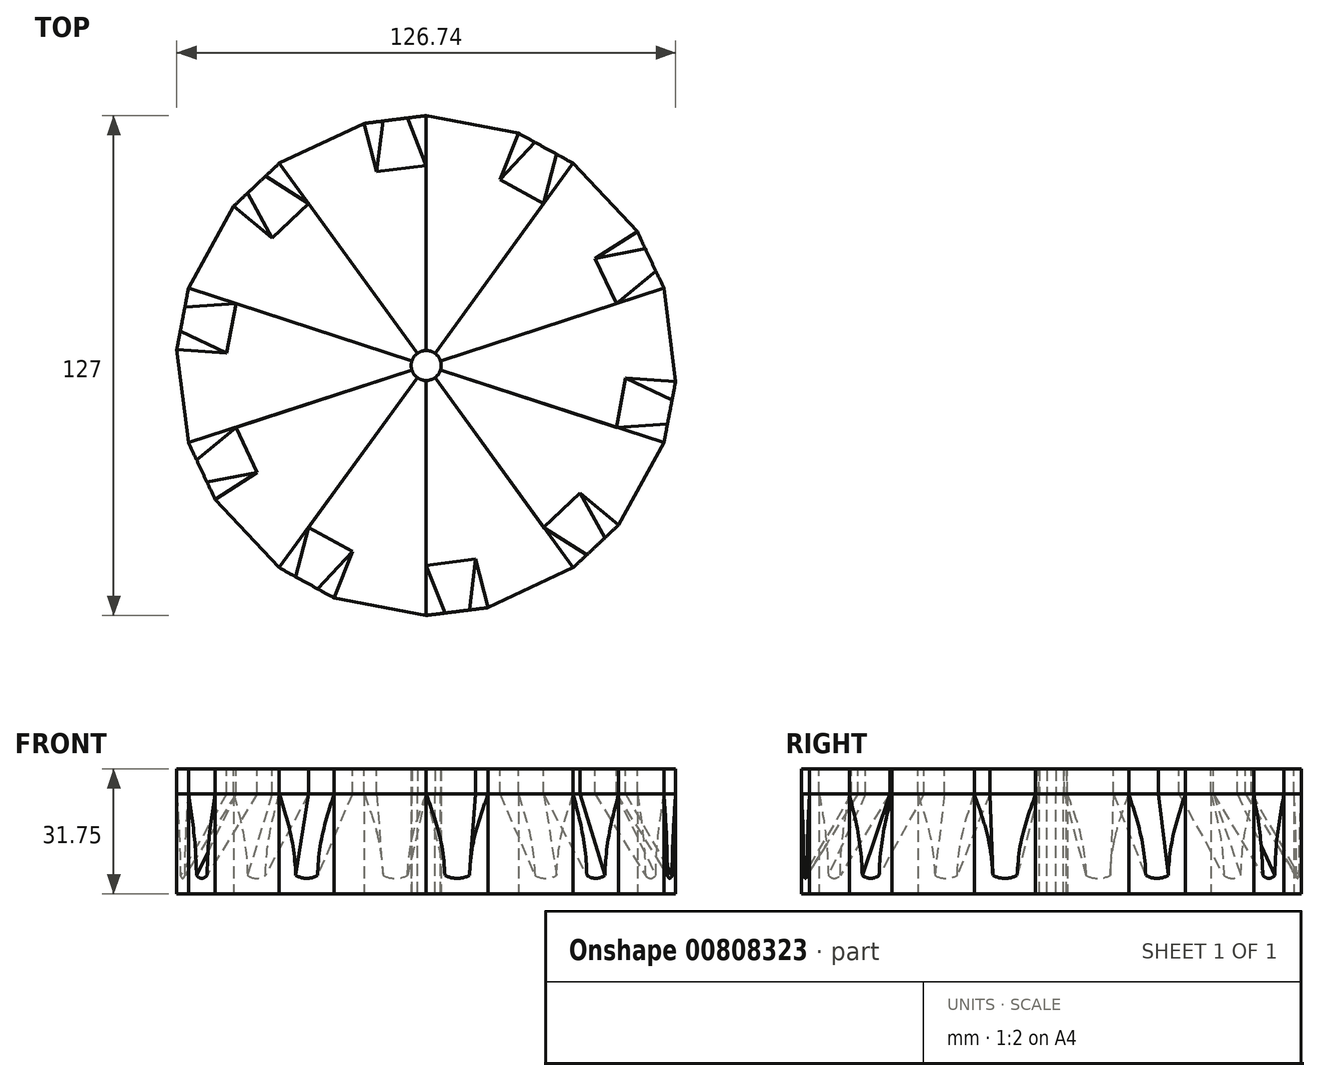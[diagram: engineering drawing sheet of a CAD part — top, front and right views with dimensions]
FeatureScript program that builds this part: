
annotation { "Feature Type Name" : "Feature", "Feature Type Description" : "" }
export const myFeature = defineFeature(function(context is Context, id is Id, definition is map)
    precondition{}
    {
        {
            var Q0;
            Q0=qCreatedBy(makeId("Top.planeOp"),FACE);
            var sketch = newSketch(context, id + "F0", { "sketchPlane" : qUnion([Q0])});
            skCircle(sketch, "E0", {"center": v(0, 0) * mm, "radius": 3.81 * mm});
            skCircle(sketch, "E1", {"center": v(0, 0) * mm, "radius": 63.5 * mm});
            skLineSegment(sketch, "E2", {"start": v(0, 0) * mm, "end": v(0, -3.81) * mm});
            skLineSegment(sketch, "E3", {"start": v(0, -50.8) * mm, "end": v(12.6, -49.21) * mm});
            skLineSegment(sketch, "E4", {"start": v(0, 0) * mm, "end": v(0.95, -3.7) * mm});
            skLineSegment(sketch, "E5", {"start": v(0, -63.5) * mm, "end": v(15.75, -61.52) * mm});
            skLineSegment(sketch, "E6.trimOffspring", {"start": v(0, -50.8) * mm, "end": v(0, -63.5) * mm});
            skLineSegment(sketch, "E7.trimOffspring", {"start": v(12.6, -49.21) * mm, "end": v(15.75, -61.52) * mm});
            skLineSegment(sketch, "E8.1.0", {"start": v(39.12, -32.4) * mm, "end": v(48.9, -40.5) * mm});
            skLineSegment(sketch, "E8.1.1", {"start": v(29.86, -41.1) * mm, "end": v(37.32, -51.37) * mm});
            skLineSegment(sketch, "E8.1.2", {"start": v(29.86, -41.1) * mm, "end": v(39.12, -32.4) * mm});
            skLineSegment(sketch, "E8.1.3", {"start": v(37.32, -51.37) * mm, "end": v(48.9, -40.5) * mm});
            skLineSegment(sketch, "E8.2.0", {"start": v(50.7, -3.22) * mm, "end": v(63.37, -4.03) * mm});
            skLineSegment(sketch, "E8.2.1", {"start": v(48.31, -15.7) * mm, "end": v(60.4, -19.62) * mm});
            skLineSegment(sketch, "E8.2.2", {"start": v(48.31, -15.7) * mm, "end": v(50.7, -3.22) * mm});
            skLineSegment(sketch, "E8.2.3", {"start": v(60.4, -19.62) * mm, "end": v(63.37, -4.03) * mm});
            skLineSegment(sketch, "E8.3.0", {"start": v(42.91, 27.2) * mm, "end": v(53.64, 33.99) * mm});
            skLineSegment(sketch, "E8.3.1", {"start": v(48.31, 15.7) * mm, "end": v(60.4, 19.62) * mm});
            skLineSegment(sketch, "E8.3.2", {"start": v(48.31, 15.7) * mm, "end": v(42.91, 27.2) * mm});
            skLineSegment(sketch, "E8.3.3", {"start": v(60.4, 19.62) * mm, "end": v(53.64, 33.99) * mm});
            skLineSegment(sketch, "E8.4.0", {"start": v(18.73, 47.22) * mm, "end": v(23.42, 59.03) * mm});
            skLineSegment(sketch, "E8.4.1", {"start": v(29.86, 41.1) * mm, "end": v(37.32, 51.37) * mm});
            skLineSegment(sketch, "E8.4.2", {"start": v(29.86, 41.1) * mm, "end": v(18.73, 47.22) * mm});
            skLineSegment(sketch, "E8.4.3", {"start": v(37.32, 51.37) * mm, "end": v(23.42, 59.03) * mm});
            skLineSegment(sketch, "E8.5.0", {"start": v(-12.6, 49.21) * mm, "end": v(-15.75, 61.52) * mm});
            skLineSegment(sketch, "E8.5.1", {"start": v(0, 50.8) * mm, "end": v(0, 63.5) * mm});
            skLineSegment(sketch, "E8.5.2", {"start": v(0, 50.8) * mm, "end": v(-12.6, 49.21) * mm});
            skLineSegment(sketch, "E8.5.3", {"start": v(0, 63.5) * mm, "end": v(-15.75, 61.52) * mm});
            skLineSegment(sketch, "E8.6.0", {"start": v(-39.12, 32.4) * mm, "end": v(-48.9, 40.5) * mm});
            skLineSegment(sketch, "E8.6.1", {"start": v(-29.86, 41.1) * mm, "end": v(-37.32, 51.37) * mm});
            skLineSegment(sketch, "E8.6.2", {"start": v(-29.86, 41.1) * mm, "end": v(-39.12, 32.4) * mm});
            skLineSegment(sketch, "E8.6.3", {"start": v(-37.32, 51.37) * mm, "end": v(-48.9, 40.5) * mm});
            skLineSegment(sketch, "E8.7.0", {"start": v(-50.7, 3.22) * mm, "end": v(-63.37, 4.03) * mm});
            skLineSegment(sketch, "E8.7.1", {"start": v(-48.31, 15.7) * mm, "end": v(-60.4, 19.62) * mm});
            skLineSegment(sketch, "E8.7.2", {"start": v(-48.31, 15.7) * mm, "end": v(-50.7, 3.22) * mm});
            skLineSegment(sketch, "E8.7.3", {"start": v(-60.4, 19.62) * mm, "end": v(-63.37, 4.03) * mm});
            skLineSegment(sketch, "E8.8.0", {"start": v(-42.91, -27.2) * mm, "end": v(-53.64, -33.99) * mm});
            skLineSegment(sketch, "E8.8.1", {"start": v(-48.31, -15.7) * mm, "end": v(-60.4, -19.62) * mm});
            skLineSegment(sketch, "E8.8.2", {"start": v(-48.31, -15.7) * mm, "end": v(-42.91, -27.2) * mm});
            skLineSegment(sketch, "E8.8.3", {"start": v(-60.4, -19.62) * mm, "end": v(-53.64, -33.99) * mm});
            skLineSegment(sketch, "E8.9.0", {"start": v(-18.73, -47.22) * mm, "end": v(-23.42, -59.03) * mm});
            skLineSegment(sketch, "E8.9.1", {"start": v(-29.86, -41.1) * mm, "end": v(-37.32, -51.37) * mm});
            skLineSegment(sketch, "E8.9.2", {"start": v(-29.86, -41.1) * mm, "end": v(-18.73, -47.22) * mm});
            skLineSegment(sketch, "E8.9.3", {"start": v(-37.32, -51.37) * mm, "end": v(-23.42, -59.03) * mm});
            skLineSegment(sketch, "E9", {"start": v(12.6, -49.21) * mm, "end": v(29.86, -41.1) * mm});
            skLineSegment(sketch, "E10", {"start": v(15.75, -61.52) * mm, "end": v(37.32, -51.37) * mm});
            skLineSegment(sketch, "E11.1.0", {"start": v(39.12, -32.4) * mm, "end": v(48.31, -15.7) * mm});
            skLineSegment(sketch, "E11.1.1", {"start": v(48.9, -40.5) * mm, "end": v(60.4, -19.62) * mm});
            skLineSegment(sketch, "E11.2.0", {"start": v(50.7, -3.22) * mm, "end": v(48.31, 15.7) * mm});
            skLineSegment(sketch, "E11.2.1", {"start": v(63.37, -4.03) * mm, "end": v(60.4, 19.62) * mm});
            skLineSegment(sketch, "E11.3.0", {"start": v(42.91, 27.2) * mm, "end": v(29.86, 41.1) * mm});
            skLineSegment(sketch, "E11.3.1", {"start": v(53.64, 33.99) * mm, "end": v(37.32, 51.37) * mm});
            skLineSegment(sketch, "E11.4.0", {"start": v(18.73, 47.22) * mm, "end": v(0, 50.8) * mm});
            skLineSegment(sketch, "E11.4.1", {"start": v(23.42, 59.03) * mm, "end": v(0, 63.5) * mm});
            skLineSegment(sketch, "E11.5.0", {"start": v(-12.6, 49.21) * mm, "end": v(-29.86, 41.1) * mm});
            skLineSegment(sketch, "E11.5.1", {"start": v(-15.75, 61.52) * mm, "end": v(-37.32, 51.37) * mm});
            skLineSegment(sketch, "E11.6.0", {"start": v(-39.12, 32.4) * mm, "end": v(-48.31, 15.7) * mm});
            skLineSegment(sketch, "E11.6.1", {"start": v(-48.9, 40.5) * mm, "end": v(-60.4, 19.62) * mm});
            skLineSegment(sketch, "E11.7.0", {"start": v(-50.7, 3.22) * mm, "end": v(-48.31, -15.7) * mm});
            skLineSegment(sketch, "E11.7.1", {"start": v(-63.37, 4.03) * mm, "end": v(-60.4, -19.62) * mm});
            skLineSegment(sketch, "E11.8.0", {"start": v(-42.91, -27.2) * mm, "end": v(-29.86, -41.1) * mm});
            skLineSegment(sketch, "E11.8.1", {"start": v(-53.64, -33.99) * mm, "end": v(-37.32, -51.37) * mm});
            skLineSegment(sketch, "E11.9.0", {"start": v(-18.73, -47.22) * mm, "end": v(0, -50.8) * mm});
            skLineSegment(sketch, "E11.9.1", {"start": v(-23.42, -59.03) * mm, "end": v(0, -63.5) * mm});
            skSolve(sketch);
        }
        {
            var Q0;
            Q0=makeQuery(id+"F0.imprint","IMPRINT",FACE,{"disambiguationData":[TD([[makeQuery(id+"F0.imprint","IMPRINT",EDGE,{"derivedFrom":sQuery(id+"F0.wireOp",EDGE,"E8.8.0")}),1.0]])]});
            var Q1;
            Q1=makeQuery(id+"F0.imprint","IMPRINT",FACE,{"disambiguationData":[TD([[makeQuery(id+"F0.imprint","IMPRINT",EDGE,{"derivedFrom":sQuery(id+"F0.wireOp",EDGE,"E8.7.0")}),1.0]])]});
            var Q2;
            Q2=makeQuery(id+"F0.imprint","IMPRINT",FACE,{"disambiguationData":[TD([[makeQuery(id+"F0.imprint","IMPRINT",EDGE,{"derivedFrom":sQuery(id+"F0.wireOp",EDGE,"E6.trimOffspring")}),-1.0]])]});
            var Q3;
            Q3=makeQuery(id+"F0.imprint","IMPRINT",FACE,{"disambiguationData":[TD([[makeQuery(id+"F0.imprint","IMPRINT",EDGE,{"derivedFrom":sQuery(id+"F0.wireOp",EDGE,"E7.trimOffspring")}),1.0]])]});
            var Q4;
            Q4=makeQuery(id+"F0.imprint","IMPRINT",FACE,{"disambiguationData":[TD([[makeQuery(id+"F0.imprint","IMPRINT",EDGE,{"derivedFrom":sQuery(id+"F0.wireOp",EDGE,"E8.1.0")}),1.0]])]});
            var Q5;
            Q5=makeQuery(id+"F0.imprint","IMPRINT",FACE,{"disambiguationData":[TD([[makeQuery(id+"F0.imprint","IMPRINT",EDGE,{"derivedFrom":sQuery(id+"F0.wireOp",EDGE,"E8.2.0")}),1.0]])]});
            var Q6;
            Q6=makeQuery(id+"F0.imprint","IMPRINT",FACE,{"disambiguationData":[TD([[makeQuery(id+"F0.imprint","IMPRINT",EDGE,{"derivedFrom":sQuery(id+"F0.wireOp",EDGE,"E8.3.0")}),1.0]])]});
            var Q7;
            Q7=makeQuery(id+"F0.imprint","IMPRINT",FACE,{"disambiguationData":[TD([[makeQuery(id+"F0.imprint","IMPRINT",EDGE,{"derivedFrom":sQuery(id+"F0.wireOp",EDGE,"E8.4.0")}),1.0]])]});
            var Q8;
            Q8=makeQuery(id+"F0.imprint","IMPRINT",FACE,{"disambiguationData":[TD([[makeQuery(id+"F0.imprint","IMPRINT",EDGE,{"derivedFrom":sQuery(id+"F0.wireOp",EDGE,"E8.5.0")}),1.0]])]});
            var Q9;
            Q9=makeQuery(id+"F0.imprint","IMPRINT",FACE,{"disambiguationData":[TD([[makeQuery(id+"F0.imprint","IMPRINT",EDGE,{"derivedFrom":sQuery(id+"F0.wireOp",EDGE,"E8.6.0")}),1.0]])]});
            var Q10;
            Q10=makeQuery(id+"F0.imprint","IMPRINT",FACE,{"disambiguationData":[TD([[makeQuery(id+"F0.imprint","IMPRINT",EDGE,{"derivedFrom":sQuery(id+"F0.wireOp",EDGE,"E3")}),1.0]])]});
            var Q11;
            Q11=makeQuery(id+"F0.imprint","IMPRINT",FACE,{"disambiguationData":[TD([[makeQuery(id+"F0.imprint","IMPRINT",EDGE,{"derivedFrom":sQuery(id+"F0.wireOp",EDGE,"E3")}),-1.0]])]});
            var Q12;
            Q12=makeQuery(id+"F0.imprint","IMPRINT",FACE,{"disambiguationData":[TD([[makeQuery(id+"F0.imprint","IMPRINT",EDGE,{"derivedFrom":sQuery(id+"F0.wireOp",EDGE,"E8.9.0")}),-1.0]])]});
            var Q13;
            Q13=makeQuery(id+"F0.imprint","IMPRINT",FACE,{"disambiguationData":[TD([[makeQuery(id+"F0.imprint","IMPRINT",EDGE,{"derivedFrom":sQuery(id+"F0.wireOp",EDGE,"E8.1.0")}),-1.0]])]});
            var Q14;
            Q14=makeQuery(id+"F0.imprint","IMPRINT",FACE,{"disambiguationData":[TD([[makeQuery(id+"F0.imprint","IMPRINT",EDGE,{"derivedFrom":sQuery(id+"F0.wireOp",EDGE,"E8.2.0")}),-1.0]])]});
            var Q15;
            Q15=makeQuery(id+"F0.imprint","IMPRINT",FACE,{"disambiguationData":[TD([[makeQuery(id+"F0.imprint","IMPRINT",EDGE,{"derivedFrom":sQuery(id+"F0.wireOp",EDGE,"E8.3.0")}),-1.0]])]});
            var Q16;
            Q16=makeQuery(id+"F0.imprint","IMPRINT",FACE,{"disambiguationData":[TD([[makeQuery(id+"F0.imprint","IMPRINT",EDGE,{"derivedFrom":sQuery(id+"F0.wireOp",EDGE,"E8.8.0")}),-1.0]])]});
            var Q17;
            Q17=makeQuery(id+"F0.imprint","IMPRINT",FACE,{"disambiguationData":[TD([[makeQuery(id+"F0.imprint","IMPRINT",EDGE,{"derivedFrom":sQuery(id+"F0.wireOp",EDGE,"E8.7.0")}),-1.0]])]});
            var Q18;
            Q18=makeQuery(id+"F0.imprint","IMPRINT",FACE,{"disambiguationData":[TD([[makeQuery(id+"F0.imprint","IMPRINT",EDGE,{"derivedFrom":sQuery(id+"F0.wireOp",EDGE,"E8.6.0")}),-1.0]])]});
            var Q19;
            Q19=makeQuery(id+"F0.imprint","IMPRINT",FACE,{"disambiguationData":[TD([[makeQuery(id+"F0.imprint","IMPRINT",EDGE,{"derivedFrom":sQuery(id+"F0.wireOp",EDGE,"E8.5.0")}),-1.0]])]});
            var Q20;
            Q20=makeQuery(id+"F0.imprint","IMPRINT",FACE,{"disambiguationData":[TD([[makeQuery(id+"F0.imprint","IMPRINT",EDGE,{"derivedFrom":sQuery(id+"F0.wireOp",EDGE,"E8.4.0")}),-1.0]])]});
            extrude(context, id + "F1", {"entities" : qUnion([Q0, Q1, Q2, Q3, Q4, Q5, Q6, Q7, Q8, Q9, Q10, Q11, Q12, Q13, Q14, Q15, Q16, Q17, Q18, Q19, Q20]), "depth" : 25.4 * mm, "offsetDistance" : 25.4 * mm});
        }
        {
            var Q0;
            Q0=makeQuery(id+"F1.opExtrude","CAP_EDGE",EDGE,{"disambiguationData":[OSD([sQuery(id+"F0.wireOp",EDGE,"E5")])],"isStart":false});
            cPoint(context, id + "F2", {"entities" : qUnion([Q0]), "parameter" : 0.5});
        }
        {
            var Q0;
            Q0=makeQuery(id+"F1.opExtrude","CAP_VERTEX",VERTEX,{"disambiguationData":[OSD([sQuery(id+"F0.wireOp",EDGE,"E1"),sQuery(id+"F0.wireOp",EDGE,"E5"),sQuery(id+"F0.wireOp",EDGE,"E7.trimOffspring"),sQuery(id+"F0.wireOp",EDGE,"E10")])],"isStart":true});
            var Q1;
            Q1=makeQuery(id+"F1.opExtrude","CAP_VERTEX",VERTEX,{"disambiguationData":[OSD([sQuery(id+"F0.wireOp",EDGE,"E1"),sQuery(id+"F0.wireOp",EDGE,"E5"),sQuery(id+"F0.wireOp",EDGE,"E6.trimOffspring"),sQuery(id+"F0.wireOp",EDGE,"E11.9.1")])],"isStart":true});
            var Q2;
            Q2 = qCreatedBy(id + "F2" ,VERTEX);
            cPlane(context, id + "F3", {"entities" : qUnion([Q0, Q1, Q2]), "cplaneType" : CPlaneType.THREE_POINT, "offset" : 25.4 * mm, "width" : 152.4 * mm, "height" : 152.4 * mm});
        }
        {
            var Q0;
            Q0=qCreatedBy(id+"F3.planeOp",FACE);
            cPlane(context, id + "F4", {"entities" : qUnion([Q0]), "cplaneType" : CPlaneType.OFFSET, "offset" : 1.59 * mm, "width" : 152.4 * mm, "height" : 152.4 * mm});
        }
        {
            var Q0;
            Q0=qCreatedBy(id+"F4.planeOp",FACE);
            var sketch = newSketch(context, id + "F5", { "sketchPlane" : qUnion([Q0])});
            skPoint(sketch, "E12.0", {"position": v(7.94, 12.7) * mm});
            skPoint(sketch, "E13.0", {"position": v(-7.94, 12.7) * mm});
            skPoint(sketch, "E14.0", {"position": v(0, 0) * mm});
            skLineSegment(sketch, "E15", {"start": v(0, 0) * mm, "end": v(0, 6.35) * mm});
            skLineSegment(sketch, "E16.bottom", {"start": v(2.74, 10.62) * mm, "end": v(-2.74, 10.62) * mm});
            skLineSegment(sketch, "E16.left", {"start": v(2.74, 10.62) * mm, "end": v(2.74, 2.08) * mm});
            skLineSegment(sketch, "E16.right", {"start": v(-2.74, 10.62) * mm, "end": v(-2.74, 2.08) * mm});
            skPoint(sketch, "E16.middle", {"position": v(0, 6.35) * mm});
            skArc(sketch, "E17.trimOffspring", {"start": v(-2.74, 2.08) * mm, "mid": v(0, 1.27) * mm, "end": v(2.74, 2.08) * mm});
            skSolve(sketch);
        }
        {
            var Q0;
            Q0=makeQuery(id+"F1.opExtrude","CAP_FACE",FACE,{"disambiguationData":[OSD([sQuery(id+"F0.wireOp",EDGE,"E0"),sQuery(id+"F0.wireOp",EDGE,"E5"),sQuery(id+"F0.wireOp",EDGE,"E8.1.3"),sQuery(id+"F0.wireOp",EDGE,"E8.2.3"),sQuery(id+"F0.wireOp",EDGE,"E8.3.3"),sQuery(id+"F0.wireOp",EDGE,"E8.4.3"),sQuery(id+"F0.wireOp",EDGE,"E8.5.3"),sQuery(id+"F0.wireOp",EDGE,"E8.6.3"),sQuery(id+"F0.wireOp",EDGE,"E8.7.3"),sQuery(id+"F0.wireOp",EDGE,"E8.8.3"),sQuery(id+"F0.wireOp",EDGE,"E8.9.3"),sQuery(id+"F0.wireOp",EDGE,"E10"),sQuery(id+"F0.wireOp",EDGE,"E11.1.1"),sQuery(id+"F0.wireOp",EDGE,"E11.2.1"),sQuery(id+"F0.wireOp",EDGE,"E11.3.1"),sQuery(id+"F0.wireOp",EDGE,"E11.4.1"),sQuery(id+"F0.wireOp",EDGE,"E11.5.1"),sQuery(id+"F0.wireOp",EDGE,"E11.6.1"),sQuery(id+"F0.wireOp",EDGE,"E11.7.1"),sQuery(id+"F0.wireOp",EDGE,"E11.8.1"),sQuery(id+"F0.wireOp",EDGE,"E11.9.1")])],"isStart":false});
            var sketch = newSketch(context, id + "F6", { "sketchPlane" : qUnion([Q0])});
            skLineSegment(sketch, "E18.0", {"start": v(37.32, -51.37) * mm, "end": v(48.9, -40.5) * mm});
            skLineSegment(sketch, "E18.1", {"start": v(29.86, -41.1) * mm, "end": v(39.12, -32.4) * mm});
            skLineSegment(sketch, "E18.2", {"start": v(-18.73, -47.22) * mm, "end": v(0, -50.8) * mm});
            skLineSegment(sketch, "E18.3", {"start": v(-48.31, 15.7) * mm, "end": v(-60.4, 19.62) * mm});
            skLineSegment(sketch, "E18.4", {"start": v(60.4, -19.62) * mm, "end": v(63.37, -4.03) * mm});
            skLineSegment(sketch, "E18.5", {"start": v(63.37, -4.03) * mm, "end": v(60.4, 19.62) * mm});
            skLineSegment(sketch, "E18.6", {"start": v(12.6, -49.21) * mm, "end": v(15.75, -61.52) * mm});
            skLineSegment(sketch, "E18.7", {"start": v(-50.7, 3.22) * mm, "end": v(-48.31, -15.7) * mm});
            skLineSegment(sketch, "E18.8", {"start": v(0, -50.8) * mm, "end": v(0, -63.5) * mm});
            skLineSegment(sketch, "E18.9", {"start": v(0, -63.5) * mm, "end": v(15.75, -61.52) * mm});
            skLineSegment(sketch, "E18.10", {"start": v(0, -50.8) * mm, "end": v(12.6, -49.21) * mm});
            skCircle(sketch, "E18.11", {"center": v(0, 0) * mm, "radius": 63.5 * mm});
            skLineSegment(sketch, "E18.12", {"start": v(50.7, -3.22) * mm, "end": v(63.37, -4.03) * mm});
            skLineSegment(sketch, "E18.13", {"start": v(42.91, 27.2) * mm, "end": v(53.64, 33.99) * mm});
            skLineSegment(sketch, "E18.14", {"start": v(48.31, -15.7) * mm, "end": v(50.7, -3.22) * mm});
            skLineSegment(sketch, "E18.15", {"start": v(-48.31, -15.7) * mm, "end": v(-42.91, -27.2) * mm});
            skLineSegment(sketch, "E18.16", {"start": v(0, 50.8) * mm, "end": v(-12.6, 49.21) * mm});
            skLineSegment(sketch, "E18.17", {"start": v(48.31, -15.7) * mm, "end": v(60.4, -19.62) * mm});
            skLineSegment(sketch, "E18.18", {"start": v(-37.32, 51.37) * mm, "end": v(-48.9, 40.5) * mm});
            skLineSegment(sketch, "E18.19", {"start": v(48.31, 15.7) * mm, "end": v(60.4, 19.62) * mm});
            skLineSegment(sketch, "E18.20", {"start": v(29.86, 41.1) * mm, "end": v(37.32, 51.37) * mm});
            skLineSegment(sketch, "E18.21", {"start": v(-12.6, 49.21) * mm, "end": v(-15.75, 61.52) * mm});
            skLineSegment(sketch, "E18.22", {"start": v(-18.73, -47.22) * mm, "end": v(-23.42, -59.03) * mm});
            skLineSegment(sketch, "E18.23", {"start": v(60.4, 19.62) * mm, "end": v(53.64, 33.99) * mm});
            skLineSegment(sketch, "E18.24", {"start": v(-39.12, 32.4) * mm, "end": v(-48.31, 15.7) * mm});
            skLineSegment(sketch, "E18.25", {"start": v(-23.42, -59.03) * mm, "end": v(0, -63.5) * mm});
            skLineSegment(sketch, "E18.26", {"start": v(-12.6, 49.21) * mm, "end": v(-29.86, 41.1) * mm});
            skLineSegment(sketch, "E18.27", {"start": v(-15.75, 61.52) * mm, "end": v(-37.32, 51.37) * mm});
            skLineSegment(sketch, "E18.28", {"start": v(-50.7, 3.22) * mm, "end": v(-63.37, 4.03) * mm});
            skLineSegment(sketch, "E18.29", {"start": v(50.7, -3.22) * mm, "end": v(48.31, 15.7) * mm});
            skLineSegment(sketch, "E18.30", {"start": v(12.6, -49.21) * mm, "end": v(29.86, -41.1) * mm});
            skLineSegment(sketch, "E18.31", {"start": v(48.9, -40.5) * mm, "end": v(60.4, -19.62) * mm});
            skLineSegment(sketch, "E18.32", {"start": v(-29.86, -41.1) * mm, "end": v(-18.73, -47.22) * mm});
            skLineSegment(sketch, "E18.33", {"start": v(-48.31, 15.7) * mm, "end": v(-50.7, 3.22) * mm});
            skLineSegment(sketch, "E18.34", {"start": v(-39.12, 32.4) * mm, "end": v(-48.9, 40.5) * mm});
            skLineSegment(sketch, "E18.35", {"start": v(42.91, 27.2) * mm, "end": v(29.86, 41.1) * mm});
            skLineSegment(sketch, "E18.36", {"start": v(-48.31, -15.7) * mm, "end": v(-60.4, -19.62) * mm});
            skLineSegment(sketch, "E18.37", {"start": v(29.86, 41.1) * mm, "end": v(18.73, 47.22) * mm});
            skLineSegment(sketch, "E18.38", {"start": v(37.32, 51.37) * mm, "end": v(23.42, 59.03) * mm});
            skLineSegment(sketch, "E18.39", {"start": v(-60.4, -19.62) * mm, "end": v(-53.64, -33.99) * mm});
            skLineSegment(sketch, "E18.40", {"start": v(-29.86, 41.1) * mm, "end": v(-39.12, 32.4) * mm});
            skLineSegment(sketch, "E18.41", {"start": v(23.42, 59.03) * mm, "end": v(0, 63.5) * mm});
            skLineSegment(sketch, "E18.42", {"start": v(39.12, -32.4) * mm, "end": v(48.31, -15.7) * mm});
            skLineSegment(sketch, "E18.43", {"start": v(39.12, -32.4) * mm, "end": v(48.9, -40.5) * mm});
            skLineSegment(sketch, "E18.44", {"start": v(-42.91, -27.2) * mm, "end": v(-29.86, -41.1) * mm});
            skLineSegment(sketch, "E18.45", {"start": v(29.86, -41.1) * mm, "end": v(37.32, -51.37) * mm});
            skLineSegment(sketch, "E18.46", {"start": v(53.64, 33.99) * mm, "end": v(37.32, 51.37) * mm});
            skCircle(sketch, "E18.47", {"center": v(0, 0) * mm, "radius": 3.81 * mm});
            skLineSegment(sketch, "E18.48", {"start": v(-48.9, 40.5) * mm, "end": v(-60.4, 19.62) * mm});
            skLineSegment(sketch, "E18.49", {"start": v(48.31, 15.7) * mm, "end": v(42.91, 27.2) * mm});
            skLineSegment(sketch, "E18.50", {"start": v(0, 50.8) * mm, "end": v(0, 63.5) * mm});
            skLineSegment(sketch, "E18.51", {"start": v(-29.86, -41.1) * mm, "end": v(-37.32, -51.37) * mm});
            skLineSegment(sketch, "E18.52", {"start": v(-29.86, 41.1) * mm, "end": v(-37.32, 51.37) * mm});
            skLineSegment(sketch, "E18.53", {"start": v(-42.91, -27.2) * mm, "end": v(-53.64, -33.99) * mm});
            skLineSegment(sketch, "E18.54", {"start": v(15.75, -61.52) * mm, "end": v(37.32, -51.37) * mm});
            skLineSegment(sketch, "E18.55", {"start": v(18.73, 47.22) * mm, "end": v(0, 50.8) * mm});
            skLineSegment(sketch, "E18.56", {"start": v(-53.64, -33.99) * mm, "end": v(-37.32, -51.37) * mm});
            skLineSegment(sketch, "E18.57", {"start": v(18.73, 47.22) * mm, "end": v(23.42, 59.03) * mm});
            skLineSegment(sketch, "E18.58", {"start": v(0, 63.5) * mm, "end": v(-15.75, 61.52) * mm});
            skLineSegment(sketch, "E18.59", {"start": v(-37.32, -51.37) * mm, "end": v(-23.42, -59.03) * mm});
            skLineSegment(sketch, "E18.60", {"start": v(-63.37, 4.03) * mm, "end": v(-60.4, -19.62) * mm});
            skLineSegment(sketch, "E18.61", {"start": v(-60.4, 19.62) * mm, "end": v(-63.37, 4.03) * mm});
            skSolve(sketch);
        }
        {
            var Q1;
            Q1=makeQuery(id+"F6.imprint","IMPRINT",FACE,{"disambiguationData":[TD([[makeQuery(id+"F6.imprint","IMPRINT",EDGE,{"derivedFrom":sQuery(id+"F6.wireOp",EDGE,"E18.6")}),-1.0]])]});
            var Q2;
            Q2=makeQuery(id+"F5.imprint","IMPRINT",FACE,{"disambiguationData":[TD([[makeQuery(id+"F5.imprint","IMPRINT",EDGE,{"derivedFrom":sQuery(id+"F5.wireOp",EDGE,"E16.bottom")}),1.0]])]});
            loft(context, id + "F7", {"operationType" : NewBodyOperationType.REMOVE, "sheetProfilesArray" : [{ "sheetProfileEntities" : qUnion([Q1]) }, { "sheetProfileEntities" : qUnion([Q2]) }]});
        }
        {
            var Q0;
            Q0=makeQuery(id+"F1.opExtrude","CAP_FACE",FACE,{"disambiguationData":[OSD([sQuery(id+"F0.wireOp",EDGE,"E0"),sQuery(id+"F0.wireOp",EDGE,"E5"),sQuery(id+"F0.wireOp",EDGE,"E8.1.3"),sQuery(id+"F0.wireOp",EDGE,"E8.2.3"),sQuery(id+"F0.wireOp",EDGE,"E8.3.3"),sQuery(id+"F0.wireOp",EDGE,"E8.4.3"),sQuery(id+"F0.wireOp",EDGE,"E8.5.3"),sQuery(id+"F0.wireOp",EDGE,"E8.6.3"),sQuery(id+"F0.wireOp",EDGE,"E8.7.3"),sQuery(id+"F0.wireOp",EDGE,"E8.8.3"),sQuery(id+"F0.wireOp",EDGE,"E8.9.3"),sQuery(id+"F0.wireOp",EDGE,"E10"),sQuery(id+"F0.wireOp",EDGE,"E11.1.1"),sQuery(id+"F0.wireOp",EDGE,"E11.2.1"),sQuery(id+"F0.wireOp",EDGE,"E11.3.1"),sQuery(id+"F0.wireOp",EDGE,"E11.4.1"),sQuery(id+"F0.wireOp",EDGE,"E11.5.1"),sQuery(id+"F0.wireOp",EDGE,"E11.6.1"),sQuery(id+"F0.wireOp",EDGE,"E11.7.1"),sQuery(id+"F0.wireOp",EDGE,"E11.8.1"),sQuery(id+"F0.wireOp",EDGE,"E11.9.1")])],"isStart":false});
            var sketch = newSketch(context, id + "F8", { "sketchPlane" : qUnion([Q0])});
            skLineSegment(sketch, "E19", {"start": v(0, -63.5) * mm, "end": v(0, 0) * mm});
            skLineSegment(sketch, "E20", {"start": v(0, 0) * mm, "end": v(37.32, -51.37) * mm});
            skSolve(sketch);
        }
        {
            var Q0;
            Q0 = qSketchRegion(id + "F8", true);
            var Q1;
            {var subQ0=sQuery(id+"F8.wireOp",EDGE,"E20");var subQ1=sQuery(id+"F8.wireOp",EDGE,"E19");var subQ2=makeQuery(id+"F8.imprint","INTERSECT",VERTEX,{"derivedFrom":[subQ1,subQ0]});Q1=makeQuery(id+"F8.imprint","IMPRINT",FACE,{"disambiguationData":[TD([[makeQuery(id+"F8.imprint","IMPRINT",EDGE,{"disambiguationData":[TD([[subQ2,1.0]])],"derivedFrom":subQ1}),1.0]])]});}
            var Q2;
            {var subQ5=makeQuery(id+"F1.opExtrude","CAP_EDGE",EDGE,{"disambiguationData":[OSD([sQuery(id+"F0.wireOp",EDGE,"E8.1.3")])],"isStart":false});Q2=makeQuery(id+"F8.imprint","IMPRINT",FACE,{"disambiguationData":[TD([[makeQuery(id+"F8.imprint","IMPRINT",EDGE,{"derivedFrom":subQ5}),1.0]])]});}
            var Q3;
            {var subQ0=sQuery(id+"F8.wireOp",EDGE,"E20");var subQ1=sQuery(id+"F8.wireOp",EDGE,"E19");var subQ2=makeQuery(id+"F8.imprint","INTERSECT",VERTEX,{"derivedFrom":[subQ1,subQ0]});Q3=makeQuery(id+"F8.imprint","IMPRINT",FACE,{"disambiguationData":[TD([[makeQuery(id+"F8.imprint","IMPRINT",EDGE,{"disambiguationData":[TD([[subQ2,1.0]])],"derivedFrom":subQ1}),-1.0]])]});}
            extrude(context, id + "F9", {"entities" : qUnion([Q0, Q1, Q2, Q3]), "operationType" : NewBodyOperationType.REMOVE, "oppositeDirection" : true, "depth" : 25.4 * mm, "offsetDistance" : 25.4 * mm});
        }
        {
            var Q0;
            Q0=makeQuery(id+"F1.opExtrude","SWEPT_BODY",BODY,{"disambiguationData":[OSD([sQuery(id+"F0.wireOp",EDGE,"E0"),sQuery(id+"F0.wireOp",EDGE,"E5"),sQuery(id+"F0.wireOp",EDGE,"E8.1.3"),sQuery(id+"F0.wireOp",EDGE,"E8.2.3"),sQuery(id+"F0.wireOp",EDGE,"E8.3.3"),sQuery(id+"F0.wireOp",EDGE,"E8.4.3"),sQuery(id+"F0.wireOp",EDGE,"E8.5.3"),sQuery(id+"F0.wireOp",EDGE,"E8.6.3"),sQuery(id+"F0.wireOp",EDGE,"E8.7.3"),sQuery(id+"F0.wireOp",EDGE,"E8.8.3"),sQuery(id+"F0.wireOp",EDGE,"E8.9.3"),sQuery(id+"F0.wireOp",EDGE,"E10"),sQuery(id+"F0.wireOp",EDGE,"E11.1.1"),sQuery(id+"F0.wireOp",EDGE,"E11.2.1"),sQuery(id+"F0.wireOp",EDGE,"E11.3.1"),sQuery(id+"F0.wireOp",EDGE,"E11.4.1"),sQuery(id+"F0.wireOp",EDGE,"E11.5.1"),sQuery(id+"F0.wireOp",EDGE,"E11.6.1"),sQuery(id+"F0.wireOp",EDGE,"E11.7.1"),sQuery(id+"F0.wireOp",EDGE,"E11.8.1"),sQuery(id+"F0.wireOp",EDGE,"E11.9.1")])]});
            var Q1;
            Q1=makeQuery(id+"F1.opExtrude","SWEPT_FACE",FACE,{"disambiguationData":[OSD([sQuery(id+"F0.wireOp",EDGE,"E0")])]});
            circularPattern(context, id + "F10", {"entities" : qUnion([Q0]), "axis" : qUnion([Q1]), "angle" : 360 * degree, "instanceCount" : 10, "equalSpace" : true});
        }
        {
            var Q0;
            Q0=makeQuery(id+"F10.opPattern","COPY",FACE,{"derivedFrom":makeQuery(id+"F1.opExtrude","CAP_FACE",FACE,{"disambiguationData":[OSD([sQuery(id+"F0.wireOp",EDGE,"E0"),sQuery(id+"F0.wireOp",EDGE,"E5"),sQuery(id+"F0.wireOp",EDGE,"E8.1.3"),sQuery(id+"F0.wireOp",EDGE,"E8.2.3"),sQuery(id+"F0.wireOp",EDGE,"E8.3.3"),sQuery(id+"F0.wireOp",EDGE,"E8.4.3"),sQuery(id+"F0.wireOp",EDGE,"E8.5.3"),sQuery(id+"F0.wireOp",EDGE,"E8.6.3"),sQuery(id+"F0.wireOp",EDGE,"E8.7.3"),sQuery(id+"F0.wireOp",EDGE,"E8.8.3"),sQuery(id+"F0.wireOp",EDGE,"E8.9.3"),sQuery(id+"F0.wireOp",EDGE,"E10"),sQuery(id+"F0.wireOp",EDGE,"E11.1.1"),sQuery(id+"F0.wireOp",EDGE,"E11.2.1"),sQuery(id+"F0.wireOp",EDGE,"E11.3.1"),sQuery(id+"F0.wireOp",EDGE,"E11.4.1"),sQuery(id+"F0.wireOp",EDGE,"E11.5.1"),sQuery(id+"F0.wireOp",EDGE,"E11.6.1"),sQuery(id+"F0.wireOp",EDGE,"E11.7.1"),sQuery(id+"F0.wireOp",EDGE,"E11.8.1"),sQuery(id+"F0.wireOp",EDGE,"E11.9.1")])],"isStart":false}),"instanceName":"7"});
            var Q1;
            Q1=makeQuery(id+"F10.opPattern","COPY",FACE,{"derivedFrom":makeQuery(id+"F1.opExtrude","CAP_FACE",FACE,{"disambiguationData":[OSD([sQuery(id+"F0.wireOp",EDGE,"E0"),sQuery(id+"F0.wireOp",EDGE,"E5"),sQuery(id+"F0.wireOp",EDGE,"E8.1.3"),sQuery(id+"F0.wireOp",EDGE,"E8.2.3"),sQuery(id+"F0.wireOp",EDGE,"E8.3.3"),sQuery(id+"F0.wireOp",EDGE,"E8.4.3"),sQuery(id+"F0.wireOp",EDGE,"E8.5.3"),sQuery(id+"F0.wireOp",EDGE,"E8.6.3"),sQuery(id+"F0.wireOp",EDGE,"E8.7.3"),sQuery(id+"F0.wireOp",EDGE,"E8.8.3"),sQuery(id+"F0.wireOp",EDGE,"E8.9.3"),sQuery(id+"F0.wireOp",EDGE,"E10"),sQuery(id+"F0.wireOp",EDGE,"E11.1.1"),sQuery(id+"F0.wireOp",EDGE,"E11.2.1"),sQuery(id+"F0.wireOp",EDGE,"E11.3.1"),sQuery(id+"F0.wireOp",EDGE,"E11.4.1"),sQuery(id+"F0.wireOp",EDGE,"E11.5.1"),sQuery(id+"F0.wireOp",EDGE,"E11.6.1"),sQuery(id+"F0.wireOp",EDGE,"E11.7.1"),sQuery(id+"F0.wireOp",EDGE,"E11.8.1"),sQuery(id+"F0.wireOp",EDGE,"E11.9.1")])],"isStart":false}),"instanceName":"6"});
            var Q2;
            Q2=makeQuery(id+"F10.opPattern","COPY",FACE,{"derivedFrom":makeQuery(id+"F1.opExtrude","CAP_FACE",FACE,{"disambiguationData":[OSD([sQuery(id+"F0.wireOp",EDGE,"E0"),sQuery(id+"F0.wireOp",EDGE,"E5"),sQuery(id+"F0.wireOp",EDGE,"E8.1.3"),sQuery(id+"F0.wireOp",EDGE,"E8.2.3"),sQuery(id+"F0.wireOp",EDGE,"E8.3.3"),sQuery(id+"F0.wireOp",EDGE,"E8.4.3"),sQuery(id+"F0.wireOp",EDGE,"E8.5.3"),sQuery(id+"F0.wireOp",EDGE,"E8.6.3"),sQuery(id+"F0.wireOp",EDGE,"E8.7.3"),sQuery(id+"F0.wireOp",EDGE,"E8.8.3"),sQuery(id+"F0.wireOp",EDGE,"E8.9.3"),sQuery(id+"F0.wireOp",EDGE,"E10"),sQuery(id+"F0.wireOp",EDGE,"E11.1.1"),sQuery(id+"F0.wireOp",EDGE,"E11.2.1"),sQuery(id+"F0.wireOp",EDGE,"E11.3.1"),sQuery(id+"F0.wireOp",EDGE,"E11.4.1"),sQuery(id+"F0.wireOp",EDGE,"E11.5.1"),sQuery(id+"F0.wireOp",EDGE,"E11.6.1"),sQuery(id+"F0.wireOp",EDGE,"E11.7.1"),sQuery(id+"F0.wireOp",EDGE,"E11.8.1"),sQuery(id+"F0.wireOp",EDGE,"E11.9.1")])],"isStart":false}),"instanceName":"5"});
            var Q3;
            Q3=makeQuery(id+"F10.opPattern","COPY",FACE,{"derivedFrom":makeQuery(id+"F1.opExtrude","CAP_FACE",FACE,{"disambiguationData":[OSD([sQuery(id+"F0.wireOp",EDGE,"E0"),sQuery(id+"F0.wireOp",EDGE,"E5"),sQuery(id+"F0.wireOp",EDGE,"E8.1.3"),sQuery(id+"F0.wireOp",EDGE,"E8.2.3"),sQuery(id+"F0.wireOp",EDGE,"E8.3.3"),sQuery(id+"F0.wireOp",EDGE,"E8.4.3"),sQuery(id+"F0.wireOp",EDGE,"E8.5.3"),sQuery(id+"F0.wireOp",EDGE,"E8.6.3"),sQuery(id+"F0.wireOp",EDGE,"E8.7.3"),sQuery(id+"F0.wireOp",EDGE,"E8.8.3"),sQuery(id+"F0.wireOp",EDGE,"E8.9.3"),sQuery(id+"F0.wireOp",EDGE,"E10"),sQuery(id+"F0.wireOp",EDGE,"E11.1.1"),sQuery(id+"F0.wireOp",EDGE,"E11.2.1"),sQuery(id+"F0.wireOp",EDGE,"E11.3.1"),sQuery(id+"F0.wireOp",EDGE,"E11.4.1"),sQuery(id+"F0.wireOp",EDGE,"E11.5.1"),sQuery(id+"F0.wireOp",EDGE,"E11.6.1"),sQuery(id+"F0.wireOp",EDGE,"E11.7.1"),sQuery(id+"F0.wireOp",EDGE,"E11.8.1"),sQuery(id+"F0.wireOp",EDGE,"E11.9.1")])],"isStart":false}),"instanceName":"4"});
            var Q4;
            Q4=makeQuery(id+"F10.opPattern","COPY",FACE,{"derivedFrom":makeQuery(id+"F1.opExtrude","CAP_FACE",FACE,{"disambiguationData":[OSD([sQuery(id+"F0.wireOp",EDGE,"E0"),sQuery(id+"F0.wireOp",EDGE,"E5"),sQuery(id+"F0.wireOp",EDGE,"E8.1.3"),sQuery(id+"F0.wireOp",EDGE,"E8.2.3"),sQuery(id+"F0.wireOp",EDGE,"E8.3.3"),sQuery(id+"F0.wireOp",EDGE,"E8.4.3"),sQuery(id+"F0.wireOp",EDGE,"E8.5.3"),sQuery(id+"F0.wireOp",EDGE,"E8.6.3"),sQuery(id+"F0.wireOp",EDGE,"E8.7.3"),sQuery(id+"F0.wireOp",EDGE,"E8.8.3"),sQuery(id+"F0.wireOp",EDGE,"E8.9.3"),sQuery(id+"F0.wireOp",EDGE,"E10"),sQuery(id+"F0.wireOp",EDGE,"E11.1.1"),sQuery(id+"F0.wireOp",EDGE,"E11.2.1"),sQuery(id+"F0.wireOp",EDGE,"E11.3.1"),sQuery(id+"F0.wireOp",EDGE,"E11.4.1"),sQuery(id+"F0.wireOp",EDGE,"E11.5.1"),sQuery(id+"F0.wireOp",EDGE,"E11.6.1"),sQuery(id+"F0.wireOp",EDGE,"E11.7.1"),sQuery(id+"F0.wireOp",EDGE,"E11.8.1"),sQuery(id+"F0.wireOp",EDGE,"E11.9.1")])],"isStart":false}),"instanceName":"3"});
            var Q5;
            Q5=makeQuery(id+"F10.opPattern","COPY",FACE,{"derivedFrom":makeQuery(id+"F1.opExtrude","CAP_FACE",FACE,{"disambiguationData":[OSD([sQuery(id+"F0.wireOp",EDGE,"E0"),sQuery(id+"F0.wireOp",EDGE,"E5"),sQuery(id+"F0.wireOp",EDGE,"E8.1.3"),sQuery(id+"F0.wireOp",EDGE,"E8.2.3"),sQuery(id+"F0.wireOp",EDGE,"E8.3.3"),sQuery(id+"F0.wireOp",EDGE,"E8.4.3"),sQuery(id+"F0.wireOp",EDGE,"E8.5.3"),sQuery(id+"F0.wireOp",EDGE,"E8.6.3"),sQuery(id+"F0.wireOp",EDGE,"E8.7.3"),sQuery(id+"F0.wireOp",EDGE,"E8.8.3"),sQuery(id+"F0.wireOp",EDGE,"E8.9.3"),sQuery(id+"F0.wireOp",EDGE,"E10"),sQuery(id+"F0.wireOp",EDGE,"E11.1.1"),sQuery(id+"F0.wireOp",EDGE,"E11.2.1"),sQuery(id+"F0.wireOp",EDGE,"E11.3.1"),sQuery(id+"F0.wireOp",EDGE,"E11.4.1"),sQuery(id+"F0.wireOp",EDGE,"E11.5.1"),sQuery(id+"F0.wireOp",EDGE,"E11.6.1"),sQuery(id+"F0.wireOp",EDGE,"E11.7.1"),sQuery(id+"F0.wireOp",EDGE,"E11.8.1"),sQuery(id+"F0.wireOp",EDGE,"E11.9.1")])],"isStart":false}),"instanceName":"2"});
            var Q6;
            Q6=makeQuery(id+"F10.opPattern","COPY",FACE,{"derivedFrom":makeQuery(id+"F1.opExtrude","CAP_FACE",FACE,{"disambiguationData":[OSD([sQuery(id+"F0.wireOp",EDGE,"E0"),sQuery(id+"F0.wireOp",EDGE,"E5"),sQuery(id+"F0.wireOp",EDGE,"E8.1.3"),sQuery(id+"F0.wireOp",EDGE,"E8.2.3"),sQuery(id+"F0.wireOp",EDGE,"E8.3.3"),sQuery(id+"F0.wireOp",EDGE,"E8.4.3"),sQuery(id+"F0.wireOp",EDGE,"E8.5.3"),sQuery(id+"F0.wireOp",EDGE,"E8.6.3"),sQuery(id+"F0.wireOp",EDGE,"E8.7.3"),sQuery(id+"F0.wireOp",EDGE,"E8.8.3"),sQuery(id+"F0.wireOp",EDGE,"E8.9.3"),sQuery(id+"F0.wireOp",EDGE,"E10"),sQuery(id+"F0.wireOp",EDGE,"E11.1.1"),sQuery(id+"F0.wireOp",EDGE,"E11.2.1"),sQuery(id+"F0.wireOp",EDGE,"E11.3.1"),sQuery(id+"F0.wireOp",EDGE,"E11.4.1"),sQuery(id+"F0.wireOp",EDGE,"E11.5.1"),sQuery(id+"F0.wireOp",EDGE,"E11.6.1"),sQuery(id+"F0.wireOp",EDGE,"E11.7.1"),sQuery(id+"F0.wireOp",EDGE,"E11.8.1"),sQuery(id+"F0.wireOp",EDGE,"E11.9.1")])],"isStart":false}),"instanceName":"1"});
            var Q7;
            Q7=makeQuery(id+"F1.opExtrude","CAP_FACE",FACE,{"disambiguationData":[OSD([sQuery(id+"F0.wireOp",EDGE,"E0"),sQuery(id+"F0.wireOp",EDGE,"E5"),sQuery(id+"F0.wireOp",EDGE,"E8.1.3"),sQuery(id+"F0.wireOp",EDGE,"E8.2.3"),sQuery(id+"F0.wireOp",EDGE,"E8.3.3"),sQuery(id+"F0.wireOp",EDGE,"E8.4.3"),sQuery(id+"F0.wireOp",EDGE,"E8.5.3"),sQuery(id+"F0.wireOp",EDGE,"E8.6.3"),sQuery(id+"F0.wireOp",EDGE,"E8.7.3"),sQuery(id+"F0.wireOp",EDGE,"E8.8.3"),sQuery(id+"F0.wireOp",EDGE,"E8.9.3"),sQuery(id+"F0.wireOp",EDGE,"E10"),sQuery(id+"F0.wireOp",EDGE,"E11.1.1"),sQuery(id+"F0.wireOp",EDGE,"E11.2.1"),sQuery(id+"F0.wireOp",EDGE,"E11.3.1"),sQuery(id+"F0.wireOp",EDGE,"E11.4.1"),sQuery(id+"F0.wireOp",EDGE,"E11.5.1"),sQuery(id+"F0.wireOp",EDGE,"E11.6.1"),sQuery(id+"F0.wireOp",EDGE,"E11.7.1"),sQuery(id+"F0.wireOp",EDGE,"E11.8.1"),sQuery(id+"F0.wireOp",EDGE,"E11.9.1")])],"isStart":false});
            var Q8;
            Q8=makeQuery(id+"F10.opPattern","COPY",FACE,{"derivedFrom":makeQuery(id+"F1.opExtrude","CAP_FACE",FACE,{"disambiguationData":[OSD([sQuery(id+"F0.wireOp",EDGE,"E0"),sQuery(id+"F0.wireOp",EDGE,"E5"),sQuery(id+"F0.wireOp",EDGE,"E8.1.3"),sQuery(id+"F0.wireOp",EDGE,"E8.2.3"),sQuery(id+"F0.wireOp",EDGE,"E8.3.3"),sQuery(id+"F0.wireOp",EDGE,"E8.4.3"),sQuery(id+"F0.wireOp",EDGE,"E8.5.3"),sQuery(id+"F0.wireOp",EDGE,"E8.6.3"),sQuery(id+"F0.wireOp",EDGE,"E8.7.3"),sQuery(id+"F0.wireOp",EDGE,"E8.8.3"),sQuery(id+"F0.wireOp",EDGE,"E8.9.3"),sQuery(id+"F0.wireOp",EDGE,"E10"),sQuery(id+"F0.wireOp",EDGE,"E11.1.1"),sQuery(id+"F0.wireOp",EDGE,"E11.2.1"),sQuery(id+"F0.wireOp",EDGE,"E11.3.1"),sQuery(id+"F0.wireOp",EDGE,"E11.4.1"),sQuery(id+"F0.wireOp",EDGE,"E11.5.1"),sQuery(id+"F0.wireOp",EDGE,"E11.6.1"),sQuery(id+"F0.wireOp",EDGE,"E11.7.1"),sQuery(id+"F0.wireOp",EDGE,"E11.8.1"),sQuery(id+"F0.wireOp",EDGE,"E11.9.1")])],"isStart":false}),"instanceName":"8"});
            var Q9;
            Q9=makeQuery(id+"F10.opPattern","COPY",FACE,{"derivedFrom":makeQuery(id+"F1.opExtrude","CAP_FACE",FACE,{"disambiguationData":[OSD([sQuery(id+"F0.wireOp",EDGE,"E0"),sQuery(id+"F0.wireOp",EDGE,"E5"),sQuery(id+"F0.wireOp",EDGE,"E8.1.3"),sQuery(id+"F0.wireOp",EDGE,"E8.2.3"),sQuery(id+"F0.wireOp",EDGE,"E8.3.3"),sQuery(id+"F0.wireOp",EDGE,"E8.4.3"),sQuery(id+"F0.wireOp",EDGE,"E8.5.3"),sQuery(id+"F0.wireOp",EDGE,"E8.6.3"),sQuery(id+"F0.wireOp",EDGE,"E8.7.3"),sQuery(id+"F0.wireOp",EDGE,"E8.8.3"),sQuery(id+"F0.wireOp",EDGE,"E8.9.3"),sQuery(id+"F0.wireOp",EDGE,"E10"),sQuery(id+"F0.wireOp",EDGE,"E11.1.1"),sQuery(id+"F0.wireOp",EDGE,"E11.2.1"),sQuery(id+"F0.wireOp",EDGE,"E11.3.1"),sQuery(id+"F0.wireOp",EDGE,"E11.4.1"),sQuery(id+"F0.wireOp",EDGE,"E11.5.1"),sQuery(id+"F0.wireOp",EDGE,"E11.6.1"),sQuery(id+"F0.wireOp",EDGE,"E11.7.1"),sQuery(id+"F0.wireOp",EDGE,"E11.8.1"),sQuery(id+"F0.wireOp",EDGE,"E11.9.1")])],"isStart":false}),"instanceName":"9"});
            extrude(context, id + "F11", {"entities" : qUnion([Q0, Q1, Q2, Q3, Q4, Q5, Q6, Q7, Q8, Q9]), "depth" : 6.35 * mm, "offsetDistance" : 25.4 * mm});
        }
    });
